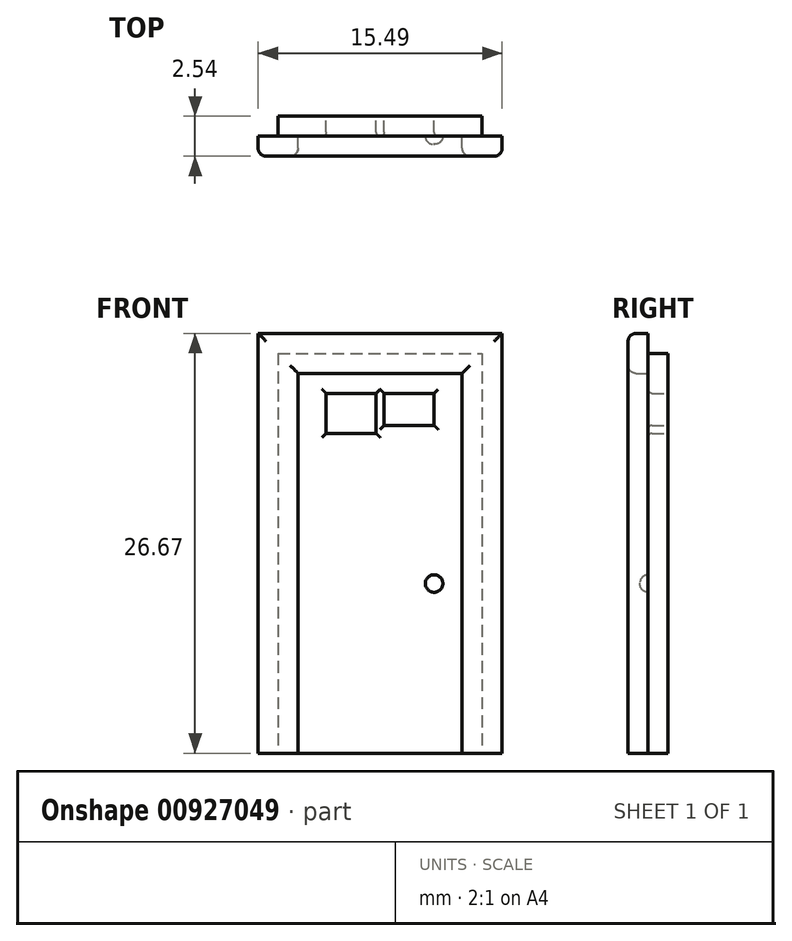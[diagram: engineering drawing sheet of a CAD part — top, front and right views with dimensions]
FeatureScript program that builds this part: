
annotation { "Feature Type Name" : "Feature", "Feature Type Description" : "" }
export const myFeature = defineFeature(function(context is Context, id is Id, definition is map)
    precondition{}
    {
        {
            var Q0;
            Q0=qCreatedBy(makeId("Front.planeOp"),FACE);
            var sketch = newSketch(context, id + "F0", { "sketchPlane" : qUnion([Q0])});
            skLineSegment(sketch, "E0.bottom", {"start": v(0, 0) * mm, "end": v(-10.41, 0) * mm});
            skLineSegment(sketch, "E0.top", {"start": v(0, 24.13) * mm, "end": v(-10.41, 24.13) * mm});
            skLineSegment(sketch, "E0.left", {"start": v(0, 0) * mm, "end": v(0, 24.13) * mm});
            skLineSegment(sketch, "E0.right", {"start": v(-10.41, 0) * mm, "end": v(-10.41, 24.13) * mm});
            skLineSegment(sketch, "E1", {"start": v(-10.41, 0) * mm, "end": v(-11.68, 0) * mm});
            skLineSegment(sketch, "E2", {"start": v(-11.68, 0) * mm, "end": v(-11.68, 25.4) * mm});
            skLineSegment(sketch, "E3", {"start": v(-11.68, 25.4) * mm, "end": v(1.27, 25.4) * mm});
            skLineSegment(sketch, "E4", {"start": v(1.27, 25.4) * mm, "end": v(1.27, 0) * mm});
            skLineSegment(sketch, "E5", {"start": v(1.27, 0) * mm, "end": v(0, 0) * mm});
            skLineSegment(sketch, "E6", {"start": v(-1.78, 22.86) * mm, "end": v(-8.64, 22.86) * mm});
            skLineSegment(sketch, "E7", {"start": v(-1.78, 22.86) * mm, "end": v(-1.78, 17.78) * mm});
            skLineSegment(sketch, "E8", {"start": v(-1.78, 17.78) * mm, "end": v(-8.64, 17.78) * mm});
            skLineSegment(sketch, "E9", {"start": v(-8.64, 22.86) * mm, "end": v(-8.64, 17.78) * mm});
            skLineSegment(sketch, "E10", {"start": v(-1.78, 22.86) * mm, "end": v(-1.78, 20.83) * mm});
            skLineSegment(sketch, "E11", {"start": v(-1.78, 20.83) * mm, "end": v(-8.64, 20.83) * mm});
            skLineSegment(sketch, "E12", {"start": v(-8.64, 20.83) * mm, "end": v(-8.64, 20.32) * mm});
            skLineSegment(sketch, "E13", {"start": v(-8.64, 20.32) * mm, "end": v(-1.78, 20.32) * mm});
            skLineSegment(sketch, "E14", {"start": v(-8.64, 17.78) * mm, "end": v(-5.46, 17.78) * mm});
            skLineSegment(sketch, "E15", {"start": v(-5.46, 17.78) * mm, "end": v(-5.46, 22.86) * mm});
            skLineSegment(sketch, "E16", {"start": v(-1.78, 17.78) * mm, "end": v(-4.95, 17.78) * mm});
            skLineSegment(sketch, "E17", {"start": v(-4.95, 17.78) * mm, "end": v(-4.95, 22.86) * mm});
            skLineSegment(sketch, "E18", {"start": v(-1.78, 0) * mm, "end": v(-1.78, 10.78) * mm});
            skCircle(sketch, "E19", {"center": v(-1.78, 10.78) * mm, "radius": 0.56 * mm});
            skSolve(sketch);
        }
        {
            var Q0;
            Q0=makeQuery(id+"F0.imprint","IMPRINT",FACE,{"disambiguationData":[TD([[makeQuery(id+"F0.imprint","IMPRINT",EDGE,{"derivedFrom":sQuery(id+"F0.wireOp",EDGE,"E0.top")}),-1.0]])]});
            extrude(context, id + "F1", {"entities" : qUnion([Q0]), "depth" : 2.54 * mm, "offsetDistance" : 25.4 * mm});
        }
        {
            var Q0;
            Q0=makeQuery(id+"F0.imprint","IMPRINT",FACE,{"disambiguationData":[TD([[makeQuery(id+"F0.imprint","IMPRINT",EDGE,{"derivedFrom":sQuery(id+"F0.wireOp",EDGE,"E0.bottom")}),-1.0]])]});
            var Q1;
            {var subQ0=sQuery(id+"F0.wireOp",EDGE,"E17");var subQ1=sQuery(id+"F0.wireOp",EDGE,"E11");var subQ2=makeQuery(id+"F0.imprint","INTERSECT",VERTEX,{"derivedFrom":[subQ1,subQ0]});Q1=makeQuery(id+"F0.imprint","IMPRINT",FACE,{"disambiguationData":[TD([[makeQuery(id+"F0.imprint","IMPRINT",EDGE,{"disambiguationData":[TD([[subQ2,-1.0]])],"derivedFrom":subQ1}),1.0]])]});}
            var Q2;
            {var subQ0=sQuery(id+"F0.wireOp",EDGE,"E15");var subQ1=sQuery(id+"F0.wireOp",EDGE,"E6");var subQ2=makeQuery(id+"F0.imprint","INTERSECT",VERTEX,{"derivedFrom":[subQ1,subQ0]});Q2=makeQuery(id+"F0.imprint","IMPRINT",FACE,{"disambiguationData":[TD([[makeQuery(id+"F0.imprint","IMPRINT",EDGE,{"disambiguationData":[TD([[subQ2,1.0]])],"derivedFrom":subQ1}),1.0]])]});}
            var Q3;
            {var subQ0=sQuery(id+"F0.wireOp",EDGE,"E12");Q3=makeQuery(id+"F0.imprint","IMPRINT",FACE,{"disambiguationData":[TD([[makeQuery(id+"F0.imprint","IMPRINT",EDGE,{"derivedFrom":subQ0}),1.0]])]});}
            var Q4;
            {var subQ0=sQuery(id+"F0.wireOp",EDGE,"E8");Q4=makeQuery(id+"F0.imprint","IMPRINT",FACE,{"disambiguationData":[TD([[makeQuery(id+"F0.imprint","IMPRINT",EDGE,{"derivedFrom":subQ0}),-1.0]])]});}
            var Q5;
            {var subQ1=sQuery(id+"F0.wireOp",EDGE,"E7");var subQ3=sQuery(id+"F0.wireOp",EDGE,"E13");var subQ4=makeQuery(id+"F0.imprint","INTERSECT",VERTEX,{"derivedFrom":[subQ1,subQ3]});Q5=makeQuery(id+"F0.imprint","IMPRINT",FACE,{"disambiguationData":[TD([[makeQuery(id+"F0.imprint","IMPRINT",EDGE,{"disambiguationData":[TD([[subQ4,1.0]])],"derivedFrom":subQ3}),1.0]])]});}
            var Q6;
            Q6=makeQuery(id+"F0.imprint","IMPRINT",FACE,{"disambiguationData":[TD([[makeQuery(id+"F0.imprint","IMPRINT",EDGE,{"derivedFrom":sQuery(id+"F0.wireOp",EDGE,"E19")}),1.0]])]});
            extrude(context, id + "F2", {"entities" : qUnion([Q0, Q1, Q2, Q3, Q4, Q5, Q6]), "operationType" : NewBodyOperationType.ADD, "depth" : 1.27 * mm, "offsetDistance" : 25.4 * mm});
        }
        {
            var Q0;
            Q0=makeQuery(id+"F0.imprint","IMPRINT",FACE,{"disambiguationData":[TD([[makeQuery(id+"F0.imprint","IMPRINT",EDGE,{"derivedFrom":sQuery(id+"F0.wireOp",EDGE,"E19")}),1.0]])]});
            extrude(context, id + "F3", {"entities" : qUnion([Q0]), "operationType" : NewBodyOperationType.ADD, "depth" : 1.78 * mm, "offsetDistance" : 25.4 * mm});
        }
        {
            var Q0;
            Q0=makeQuery(id+"F1.opExtrude","CAP_EDGE",EDGE,{"disambiguationData":[OSD([sQuery(id+"F0.wireOp",EDGE,"E0.right")])],"isStart":false});
            var Q1;
            Q1=makeQuery(id+"F1.opExtrude","CAP_EDGE",EDGE,{"disambiguationData":[OSD([sQuery(id+"F0.wireOp",EDGE,"E0.left")])],"isStart":false});
            var Q2;
            Q2=makeQuery(id+"F1.opExtrude","CAP_EDGE",EDGE,{"disambiguationData":[OSD([sQuery(id+"F0.wireOp",EDGE,"E0.top")])],"isStart":false});
            var Q3;
            Q3=makeQuery(id+"F3.opExtrude","CAP_EDGE",EDGE,{"disambiguationData":[OSD([sQuery(id+"F0.wireOp",EDGE,"E19")])],"isStart":false});
            fillet(context, id + "F4", {"entities" : qUnion([Q0, Q1, Q2, Q3]), "radius" : 0.5 * mm, "tangentPropagation" : true, "allowEdgeOverflow" : false});
        }
        {
            var Q0;
            {var subQ0=sQuery(id+"F0.wireOp",EDGE,"E6");Q0=makeQuery(id+"F2.opExtrude","CAP_EDGE",EDGE,{"disambiguationData":[OSD([subQ0]),TDD([makeQuery(id+"F0.imprint","IMPRINT",EDGE,{"disambiguationData":[TD([[makeQuery(id+"F0.imprint","INTERSECT",VERTEX,{"derivedFrom":[subQ0,sQuery(id+"F0.wireOp",EDGE,"E10")]}),-1.0]])],"derivedFrom":subQ0})])],"isStart":false});}
            var Q1;
            Q1=makeQuery(id+"F2.opExtrude","CAP_EDGE",EDGE,{"disambiguationData":[OSD([sQuery(id+"F0.wireOp",EDGE,"E10")])],"isStart":false});
            var Q2;
            {var subQ0=sQuery(id+"F0.wireOp",EDGE,"E11");Q2=makeQuery(id+"F2.opExtrude","CAP_EDGE",EDGE,{"disambiguationData":[OSD([subQ0]),TDD([makeQuery(id+"F0.imprint","IMPRINT",EDGE,{"disambiguationData":[TD([[makeQuery(id+"F0.imprint","INTERSECT",VERTEX,{"derivedFrom":[subQ0,sQuery(id+"F0.wireOp",EDGE,"E17")]}),1.0]])],"derivedFrom":subQ0})])],"isStart":false});}
            var Q3;
            Q3=makeQuery(id+"F2.opExtrude","CAP_EDGE",EDGE,{"disambiguationData":[OSD([sQuery(id+"F0.wireOp",EDGE,"E7")])],"isStart":false});
            var Q4;
            Q4=makeQuery(id+"F2.opExtrude","CAP_EDGE",EDGE,{"disambiguationData":[OSD([sQuery(id+"F0.wireOp",EDGE,"E16")])],"isStart":false});
            var Q5;
            Q5=makeQuery(id+"F2.opExtrude","CAP_EDGE",EDGE,{"disambiguationData":[OSD([sQuery(id+"F0.wireOp",EDGE,"E14")])],"isStart":false});
            var Q6;
            {var subQ0=sQuery(id+"F0.wireOp",EDGE,"E15");Q6=makeQuery(id+"F2.opExtrude","CAP_EDGE",EDGE,{"disambiguationData":[OSD([subQ0]),TDD([makeQuery(id+"F0.imprint","IMPRINT",EDGE,{"disambiguationData":[TD([[makeQuery(id+"F0.imprint","INTERSECT",VERTEX,{"derivedFrom":[sQuery(id+"F0.wireOp",EDGE,"E13"),subQ0]}),1.0]])],"derivedFrom":subQ0})])],"isStart":false});}
            var Q7;
            {var subQ0=sQuery(id+"F0.wireOp",EDGE,"E6");Q7=makeQuery(id+"F2.opExtrude","CAP_EDGE",EDGE,{"disambiguationData":[OSD([subQ0]),TDD([makeQuery(id+"F0.imprint","IMPRINT",EDGE,{"disambiguationData":[TD([[makeQuery(id+"F0.imprint","INTERSECT",VERTEX,{"derivedFrom":[subQ0,sQuery(id+"F0.wireOp",EDGE,"E9")]}),1.0]])],"derivedFrom":subQ0})])],"isStart":false});}
            var Q8;
            {var subQ0=sQuery(id+"F0.wireOp",EDGE,"E9");Q8=makeQuery(id+"F2.opExtrude","CAP_EDGE",EDGE,{"disambiguationData":[OSD([subQ0]),TDD([makeQuery(id+"F0.imprint","IMPRINT",EDGE,{"disambiguationData":[TD([[makeQuery(id+"F0.imprint","INTERSECT",VERTEX,{"derivedFrom":[sQuery(id+"F0.wireOp",EDGE,"E6"),subQ0]}),-1.0]])],"derivedFrom":subQ0})])],"isStart":false});}
            var Q9;
            {var subQ0=sQuery(id+"F0.wireOp",EDGE,"E9");Q9=makeQuery(id+"F2.opExtrude","CAP_EDGE",EDGE,{"disambiguationData":[OSD([subQ0]),TDD([makeQuery(id+"F0.imprint","IMPRINT",EDGE,{"disambiguationData":[TD([[makeQuery(id+"F0.imprint","INTERSECT",VERTEX,{"derivedFrom":[subQ0,sQuery(id+"F0.wireOp",EDGE,"E14")]}),1.0]])],"derivedFrom":subQ0})])],"isStart":false});}
            var Q10;
            {var subQ0=sQuery(id+"F0.wireOp",EDGE,"E13");Q10=makeQuery(id+"F2.opExtrude","CAP_EDGE",EDGE,{"disambiguationData":[OSD([subQ0]),TDD([makeQuery(id+"F0.imprint","IMPRINT",EDGE,{"disambiguationData":[TD([[makeQuery(id+"F0.imprint","INTERSECT",VERTEX,{"derivedFrom":[subQ0,sQuery(id+"F0.wireOp",EDGE,"E15")]}),1.0]])],"derivedFrom":subQ0})])],"isStart":false});}
            var Q11;
            {var subQ0=sQuery(id+"F0.wireOp",EDGE,"E17");Q11=makeQuery(id+"F2.opExtrude","CAP_EDGE",EDGE,{"disambiguationData":[OSD([subQ0]),TDD([makeQuery(id+"F0.imprint","IMPRINT",EDGE,{"disambiguationData":[TD([[makeQuery(id+"F0.imprint","INTERSECT",VERTEX,{"derivedFrom":[sQuery(id+"F0.wireOp",EDGE,"E6"),subQ0]}),1.0]])],"derivedFrom":subQ0})])],"isStart":false});}
            var Q12;
            {var subQ0=sQuery(id+"F0.wireOp",EDGE,"E11");Q12=makeQuery(id+"F2.opExtrude","CAP_EDGE",EDGE,{"disambiguationData":[OSD([subQ0]),TDD([makeQuery(id+"F0.imprint","IMPRINT",EDGE,{"disambiguationData":[TD([[makeQuery(id+"F0.imprint","INTERSECT",VERTEX,{"derivedFrom":[subQ0,sQuery(id+"F0.wireOp",EDGE,"E15")]}),-1.0]])],"derivedFrom":subQ0})])],"isStart":false});}
            var Q13;
            {var subQ0=sQuery(id+"F0.wireOp",EDGE,"E15");Q13=makeQuery(id+"F2.opExtrude","CAP_EDGE",EDGE,{"disambiguationData":[OSD([subQ0]),TDD([makeQuery(id+"F0.imprint","IMPRINT",EDGE,{"disambiguationData":[TD([[makeQuery(id+"F0.imprint","INTERSECT",VERTEX,{"derivedFrom":[sQuery(id+"F0.wireOp",EDGE,"E6"),subQ0]}),1.0]])],"derivedFrom":subQ0})])],"isStart":false});}
            var Q14;
            {var subQ0=sQuery(id+"F0.wireOp",EDGE,"E17");Q14=makeQuery(id+"F2.opExtrude","CAP_EDGE",EDGE,{"disambiguationData":[OSD([subQ0]),TDD([makeQuery(id+"F0.imprint","IMPRINT",EDGE,{"disambiguationData":[TD([[makeQuery(id+"F0.imprint","INTERSECT",VERTEX,{"derivedFrom":[sQuery(id+"F0.wireOp",EDGE,"E13"),subQ0]}),1.0]])],"derivedFrom":subQ0})])],"isStart":false});}
            var Q15;
            {var subQ0=sQuery(id+"F0.wireOp",EDGE,"E13");Q15=makeQuery(id+"F2.opExtrude","CAP_EDGE",EDGE,{"disambiguationData":[OSD([subQ0]),TDD([makeQuery(id+"F0.imprint","IMPRINT",EDGE,{"disambiguationData":[TD([[makeQuery(id+"F0.imprint","INTERSECT",VERTEX,{"derivedFrom":[sQuery(id+"F0.wireOp",EDGE,"E7"),subQ0]}),1.0]])],"derivedFrom":subQ0})])],"isStart":false});}
            fillet(context, id + "F5", {"entities" : qUnion([Q0, Q1, Q2, Q3, Q4, Q5, Q6, Q7, Q8, Q9, Q10, Q11, Q12, Q13, Q14, Q15]), "radius" : 0.25 * mm, "tangentPropagation" : true, "allowEdgeOverflow" : false});
        }
        {
            var Q0;
            Q0=makeQuery(id+"F1.opExtrude","SWEPT_FACE",FACE,{"disambiguationData":[OSD([sQuery(id+"F0.wireOp",EDGE,"E4")])]});
            var sketch = newSketch(context, id + "F6", { "sketchPlane" : qUnion([Q0])});
            skLineSegment(sketch, "E20.bottom", {"start": v(-2.54, 25.4) * mm, "end": v(-1.27, 25.4) * mm});
            skLineSegment(sketch, "E20.top", {"start": v(-2.54, 0) * mm, "end": v(-1.27, 0) * mm});
            skLineSegment(sketch, "E20.left", {"start": v(-2.54, 25.4) * mm, "end": v(-2.54, 0) * mm});
            skLineSegment(sketch, "E20.right", {"start": v(-1.27, 25.4) * mm, "end": v(-1.27, 0) * mm});
            skSolve(sketch);
        }
        {
            var Q0;
            Q0=makeQuery(id+"F6.imprint","IMPRINT",FACE,{"disambiguationData":[TD([[makeQuery(id+"F6.imprint","IMPRINT",EDGE,{"derivedFrom":sQuery(id+"F6.wireOp",EDGE,"E20.bottom")}),-1.0]])]});
            extrude(context, id + "F7", {"entities" : qUnion([Q0]), "operationType" : NewBodyOperationType.ADD, "depth" : 1.27 * mm, "offsetDistance" : 25.4 * mm});
        }
        {
            var Q0;
            Q0=makeQuery(id+"F1.opExtrude","SWEPT_FACE",FACE,{"disambiguationData":[OSD([sQuery(id+"F0.wireOp",EDGE,"E2")])]});
            var sketch = newSketch(context, id + "F8", { "sketchPlane" : qUnion([Q0])});
            skLineSegment(sketch, "E21.bottom", {"start": v(2.54, 25.4) * mm, "end": v(1.27, 25.4) * mm});
            skLineSegment(sketch, "E21.top", {"start": v(2.54, 0) * mm, "end": v(1.27, 0) * mm});
            skLineSegment(sketch, "E21.left", {"start": v(2.54, 25.4) * mm, "end": v(2.54, 0) * mm});
            skLineSegment(sketch, "E21.right", {"start": v(1.27, 25.4) * mm, "end": v(1.27, 0) * mm});
            skSolve(sketch);
        }
        {
            var Q0;
            Q0=makeQuery(id+"F8.imprint","IMPRINT",FACE,{"disambiguationData":[TD([[makeQuery(id+"F8.imprint","IMPRINT",EDGE,{"derivedFrom":sQuery(id+"F8.wireOp",EDGE,"E21.bottom")}),1.0]])]});
            extrude(context, id + "F9", {"entities" : qUnion([Q0]), "operationType" : NewBodyOperationType.ADD, "depth" : 1.27 * mm, "offsetDistance" : 25.4 * mm});
        }
        {
            var Q0;
            Q0=makeQuery(id+"F9.boolean.opBoolean","MERGE",FACE,{"derivedFrom":[makeQuery(id+"F7.boolean.opBoolean","MERGE",FACE,{"derivedFrom":[makeQuery(id+"F1.opExtrude","SWEPT_FACE",FACE,{"disambiguationData":[OSD([sQuery(id+"F0.wireOp",EDGE,"E3")])]}),makeQuery(id+"F7.opExtrude","SWEPT_FACE",FACE,{"disambiguationData":[OSD([sQuery(id+"F6.wireOp",EDGE,"E20.bottom")])]})]}),makeQuery(id+"F9.opExtrude","SWEPT_FACE",FACE,{"disambiguationData":[OSD([sQuery(id+"F8.wireOp",EDGE,"E21.bottom")])]})]});
            var sketch = newSketch(context, id + "F10", { "sketchPlane" : qUnion([Q0])});
            skLineSegment(sketch, "E22.bottom", {"start": v(-12.95, -2.54) * mm, "end": v(2.54, -2.54) * mm});
            skLineSegment(sketch, "E22.top", {"start": v(-12.95, -1.27) * mm, "end": v(2.54, -1.27) * mm});
            skLineSegment(sketch, "E22.left", {"start": v(-12.95, -2.54) * mm, "end": v(-12.95, -1.27) * mm});
            skLineSegment(sketch, "E22.right", {"start": v(2.54, -2.54) * mm, "end": v(2.54, -1.27) * mm});
            skSolve(sketch);
        }
        {
            var Q0;
            Q0=makeQuery(id+"F10.imprint","IMPRINT",FACE,{"disambiguationData":[TD([[makeQuery(id+"F10.imprint","IMPRINT",EDGE,{"derivedFrom":sQuery(id+"F10.wireOp",EDGE,"E22.bottom")}),1.0]])]});
            extrude(context, id + "F11", {"entities" : qUnion([Q0]), "operationType" : NewBodyOperationType.ADD, "depth" : 1.27 * mm, "offsetDistance" : 25.4 * mm});
        }
        {
            var Q0;
            Q0=makeQuery(id+"F11.boolean.opBoolean","MERGE",EDGE,{"derivedFrom":[makeQuery(id+"F9.opExtrude","CAP_EDGE",EDGE,{"disambiguationData":[OSD([sQuery(id+"F8.wireOp",EDGE,"E21.left")])],"isStart":false}),makeQuery(id+"F11.opExtrude","SWEPT_EDGE",EDGE,{"disambiguationData":[OSD([sQuery(id+"F10.wireOp",EDGE,"E22.bottom"),sQuery(id+"F10.wireOp",EDGE,"E22.left")])]})]});
            var Q1;
            Q1=makeQuery(id+"F11.opExtrude","CAP_EDGE",EDGE,{"disambiguationData":[OSD([sQuery(id+"F10.wireOp",EDGE,"E22.bottom")])],"isStart":false});
            var Q2;
            Q2=makeQuery(id+"F11.boolean.opBoolean","MERGE",EDGE,{"derivedFrom":[makeQuery(id+"F7.opExtrude","CAP_EDGE",EDGE,{"disambiguationData":[OSD([sQuery(id+"F6.wireOp",EDGE,"E20.left")])],"isStart":false}),makeQuery(id+"F11.opExtrude","SWEPT_EDGE",EDGE,{"disambiguationData":[OSD([sQuery(id+"F10.wireOp",EDGE,"E22.bottom"),sQuery(id+"F10.wireOp",EDGE,"E22.right")])]})]});
            fillet(context, id + "F12", {"entities" : qUnion([Q0, Q1, Q2]), "radius" : 0.5 * mm, "tangentPropagation" : true, "allowEdgeOverflow" : false});
        }
    });
